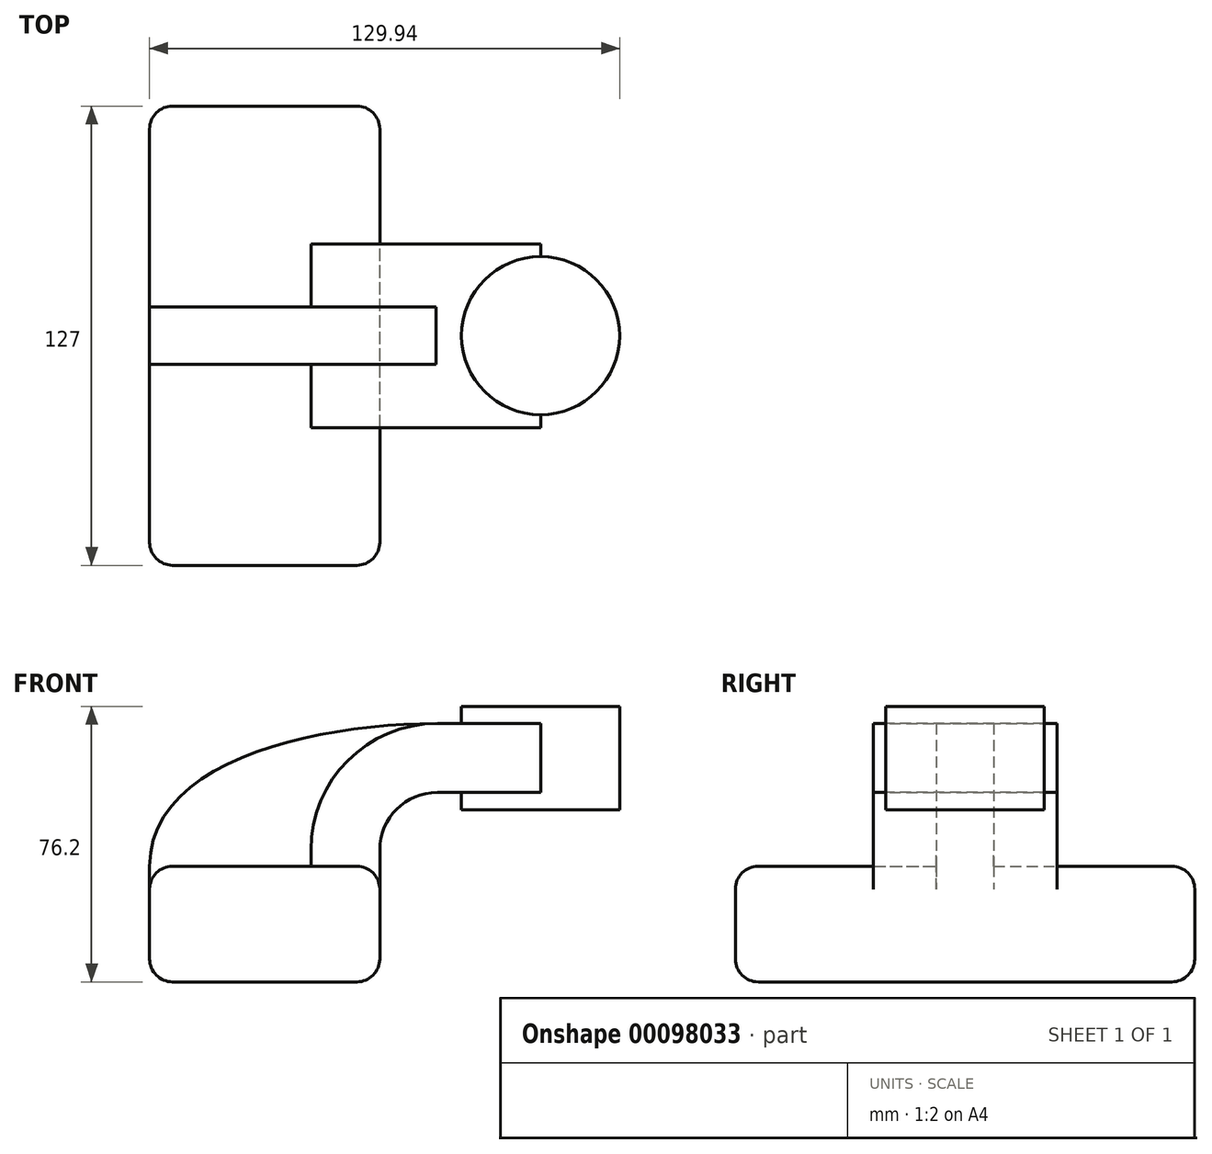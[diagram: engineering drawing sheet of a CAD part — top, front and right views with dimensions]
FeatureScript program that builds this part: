
annotation { "Feature Type Name" : "Feature", "Feature Type Description" : "" }
export const myFeature = defineFeature(function(context is Context, id is Id, definition is map)
    precondition{}
    {
        {
            var Q0;
            Q0=qCreatedBy(makeId("Front.planeOp"),FACE);
            var sketch = newSketch(context, id + "F0", { "sketchPlane" : qUnion([Q0])});
            skLineSegment(sketch, "E0.bottom", {"start": v(-31.82, 16) * mm, "end": v(31.82, 16) * mm});
            skLineSegment(sketch, "E0.top", {"start": v(-31.82, -16) * mm, "end": v(31.82, -16) * mm});
            skLineSegment(sketch, "E0.left", {"start": v(-31.82, 16) * mm, "end": v(-31.82, -16) * mm});
            skLineSegment(sketch, "E0.right", {"start": v(31.82, 16) * mm, "end": v(31.82, -16) * mm});
            skPoint(sketch, "E0.middle", {"position": v(0, 0) * mm});
            skLineSegment(sketch, "E1.bottom", {"start": v(98.12, 31.62) * mm, "end": v(47.32, 31.62) * mm});
            skLineSegment(sketch, "E1.top", {"start": v(98.12, 60.2) * mm, "end": v(47.32, 60.2) * mm});
            skLineSegment(sketch, "E1.left", {"start": v(98.12, 31.62) * mm, "end": v(98.12, 60.2) * mm});
            skLineSegment(sketch, "E1.right", {"start": v(47.32, 31.62) * mm, "end": v(47.32, 60.2) * mm});
            skPoint(sketch, "E1.middle", {"position": v(72.72, 45.91) * mm});
            skLineSegment(sketch, "E2", {"start": v(31.82, 16) * mm, "end": v(31.82, 20.52) * mm});
            skArc(sketch, "E3", {"start": v(31.82, 20.52) * mm, "mid": v(36.47, 31.75) * mm, "end": v(47.7, 36.4) * mm});
            skLineSegment(sketch, "E4", {"start": v(47.7, 36.4) * mm, "end": v(76.27, 36.4) * mm});
            skLineSegment(sketch, "E5.0", {"start": v(47.7, 55.45) * mm, "end": v(76.27, 55.45) * mm});
            skArc(sketch, "E5.1", {"start": v(12.77, 20.52) * mm, "mid": v(23, 45.22) * mm, "end": v(47.7, 55.45) * mm});
            skLineSegment(sketch, "E5.2", {"start": v(12.77, 16) * mm, "end": v(12.77, 20.52) * mm});
            skLineSegment(sketch, "E6", {"start": v(76.27, 60.2) * mm, "end": v(76.27, 31.62) * mm});
            skFitSpline(sketch, "E7", {"points": [v(47.7, 55.45) * mm, v(-31.82, 16) * mm], "startDerivative": vector(-97.87, 0) * mm, "endDerivative": vector(0, -88.76) * mm});
            skSolve(sketch);
        }
        {
            var Q0;
            Q0=makeQuery(id+"F0.imprint","IMPRINT",FACE,{"disambiguationData":[TD([[makeQuery(id+"F0.imprint","IMPRINT",EDGE,{"derivedFrom":sQuery(id+"F0.wireOp",EDGE,"E0.top")}),1.0]])]});
            extrude(context, id + "F1", {"entities" : qUnion([Q0]), "endBound" : BoundingType.SYMMETRIC, "depth" : 127 * mm});
        }
        {
            var Q0;
            {var subQ1=sQuery(id+"F0.wireOp",EDGE,"E2");Q0=makeQuery(id+"F0.imprint","IMPRINT",FACE,{"disambiguationData":[TD([[makeQuery(id+"F0.imprint","IMPRINT",EDGE,{"derivedFrom":subQ1}),1.0]])]});}
            var Q1;
            {var subQ1=sQuery(id+"F0.wireOp",EDGE,"E4");Q1=makeQuery(id+"F0.imprint","IMPRINT",FACE,{"disambiguationData":[TD([[makeQuery(id+"F0.imprint","IMPRINT",EDGE,{"derivedFrom":subQ1}),1.0]])]});}
            extrude(context, id + "F2", {"entities" : qUnion([Q0, Q1]), "operationType" : NewBodyOperationType.ADD, "endBound" : BoundingType.SYMMETRIC, "depth" : 50.8 * mm});
        }
        {
            var Q0;
            {var subQ0=sQuery(id+"F0.wireOp",EDGE,"E5.2");Q0=makeQuery(id+"F0.imprint","IMPRINT",FACE,{"disambiguationData":[TD([[makeQuery(id+"F0.imprint","IMPRINT",EDGE,{"derivedFrom":subQ0}),1.0]])]});}
            extrude(context, id + "F3", {"entities" : qUnion([Q0]), "operationType" : NewBodyOperationType.ADD, "endBound" : BoundingType.SYMMETRIC, "depth" : 15.88 * mm});
        }
        {
            var Q0;
            {var subQ0=sQuery(id+"F0.wireOp",EDGE,"E1.left");Q0=makeQuery(id+"F0.imprint","IMPRINT",FACE,{"disambiguationData":[TD([[makeQuery(id+"F0.imprint","IMPRINT",EDGE,{"derivedFrom":subQ0}),1.0]])]});}
            var Q1;
            Q1=sQuery(id+"F0.wireOp",EDGE,"E6");
            revolve(context, id + "F4", {"operationType" : NewBodyOperationType.ADD, "entities" : qUnion([Q0]), "axis" : qUnion([Q1]), "revolveType" : RevolveType.FULL});
        }
        {
            var Q0;
            Q0=makeQuery(id+"F1.opExtrude","CAP_EDGE",EDGE,{"disambiguationData":[OSD([sQuery(id+"F0.wireOp",EDGE,"E0.right")])],"isStart":false});
            var Q1;
            Q1=makeQuery(id+"F1.opExtrude","CAP_EDGE",EDGE,{"disambiguationData":[OSD([sQuery(id+"F0.wireOp",EDGE,"E0.left")])],"isStart":false});
            var Q2;
            Q2=makeQuery(id+"F1.opExtrude","CAP_EDGE",EDGE,{"disambiguationData":[OSD([sQuery(id+"F0.wireOp",EDGE,"E0.left")])],"isStart":true});
            var Q3;
            Q3=makeQuery(id+"F1.opExtrude","CAP_EDGE",EDGE,{"disambiguationData":[OSD([sQuery(id+"F0.wireOp",EDGE,"E0.right")])],"isStart":true});
            var Q4;
            Q4=makeQuery(id+"F1.opExtrude","CAP_EDGE",EDGE,{"disambiguationData":[OSD([sQuery(id+"F0.wireOp",EDGE,"E0.bottom")])],"isStart":false});
            var Q5;
            Q5=makeQuery(id+"F1.opExtrude","CAP_EDGE",EDGE,{"disambiguationData":[OSD([sQuery(id+"F0.wireOp",EDGE,"E0.top")])],"isStart":false});
            var Q6;
            {var subQ0=sQuery(id+"F0.wireOp",EDGE,"E2");var subQ1=sQuery(id+"F0.wireOp",EDGE,"E0.bottom");var subQ2=sQuery(id+"F0.wireOp",EDGE,"E0.right");Q6=makeQuery(id+"F2.boolean.opBoolean","SPLIT",EDGE,{"disambiguationData":[TD([makeQuery(id+"F1.opExtrude","CAP_FACE",FACE,{"disambiguationData":[OSD([subQ1,sQuery(id+"F0.wireOp",EDGE,"E0.top"),sQuery(id+"F0.wireOp",EDGE,"E0.left"),subQ2])],"isStart":false})])],"derivedFrom":makeQuery(id+"F1.opExtrude","SWEPT_EDGE",EDGE,{"disambiguationData":[OSD([subQ1,subQ2,subQ0])]})});}
            var Q7;
            Q7=makeQuery(id+"F1.opExtrude","SWEPT_EDGE",EDGE,{"disambiguationData":[OSD([sQuery(id+"F0.wireOp",EDGE,"E0.top"),sQuery(id+"F0.wireOp",EDGE,"E0.right")])]});
            var Q8;
            {var subQ0=sQuery(id+"F0.wireOp",EDGE,"E0.left");var subQ1=sQuery(id+"F0.wireOp",EDGE,"E7");var subQ2=sQuery(id+"F0.wireOp",EDGE,"E0.bottom");Q8=makeQuery(id+"F3.boolean.opBoolean","SPLIT",EDGE,{"disambiguationData":[TD([makeQuery(id+"F1.opExtrude","CAP_FACE",FACE,{"disambiguationData":[OSD([subQ2,sQuery(id+"F0.wireOp",EDGE,"E0.top"),subQ0,sQuery(id+"F0.wireOp",EDGE,"E0.right")])],"isStart":true})])],"derivedFrom":makeQuery(id+"F1.opExtrude","SWEPT_EDGE",EDGE,{"disambiguationData":[OSD([subQ2,subQ0,subQ1])]})});}
            var Q9;
            {var subQ0=sQuery(id+"F0.wireOp",EDGE,"E0.left");var subQ1=sQuery(id+"F0.wireOp",EDGE,"E0.bottom");var subQ2=sQuery(id+"F0.wireOp",EDGE,"E7");Q9=makeQuery(id+"F3.boolean.opBoolean","SPLIT",EDGE,{"disambiguationData":[TD([makeQuery(id+"F1.opExtrude","CAP_FACE",FACE,{"disambiguationData":[OSD([subQ1,sQuery(id+"F0.wireOp",EDGE,"E0.top"),subQ0,sQuery(id+"F0.wireOp",EDGE,"E0.right")])],"isStart":false})])],"derivedFrom":makeQuery(id+"F1.opExtrude","SWEPT_EDGE",EDGE,{"disambiguationData":[OSD([subQ1,subQ0,subQ2])]})});}
            var Q10;
            Q10=makeQuery(id+"F1.opExtrude","SWEPT_EDGE",EDGE,{"disambiguationData":[OSD([sQuery(id+"F0.wireOp",EDGE,"E0.top"),sQuery(id+"F0.wireOp",EDGE,"E0.left")])]});
            var Q11;
            Q11=makeQuery(id+"F1.opExtrude","CAP_EDGE",EDGE,{"disambiguationData":[OSD([sQuery(id+"F0.wireOp",EDGE,"E0.bottom")])],"isStart":true});
            var Q12;
            Q12=makeQuery(id+"F1.opExtrude","CAP_EDGE",EDGE,{"disambiguationData":[OSD([sQuery(id+"F0.wireOp",EDGE,"E0.top")])],"isStart":true});
            var Q13;
            {var subQ0=sQuery(id+"F0.wireOp",EDGE,"E2");var subQ1=sQuery(id+"F0.wireOp",EDGE,"E0.bottom");var subQ2=sQuery(id+"F0.wireOp",EDGE,"E0.right");Q13=makeQuery(id+"F2.boolean.opBoolean","SPLIT",EDGE,{"disambiguationData":[TD([makeQuery(id+"F1.opExtrude","CAP_FACE",FACE,{"disambiguationData":[OSD([subQ1,sQuery(id+"F0.wireOp",EDGE,"E0.top"),sQuery(id+"F0.wireOp",EDGE,"E0.left"),subQ2])],"isStart":true})])],"derivedFrom":makeQuery(id+"F1.opExtrude","SWEPT_EDGE",EDGE,{"disambiguationData":[OSD([subQ1,subQ2,subQ0])]})});}
            fillet(context, id + "F5", {"entities" : qUnion([Q0, Q1, Q2, Q3, Q4, Q5, Q6, Q7, Q8, Q9, Q10, Q11, Q12, Q13]), "radius" : 6.35 * mm, "tangentPropagation" : true, "allowEdgeOverflow" : false});
        }
    });
